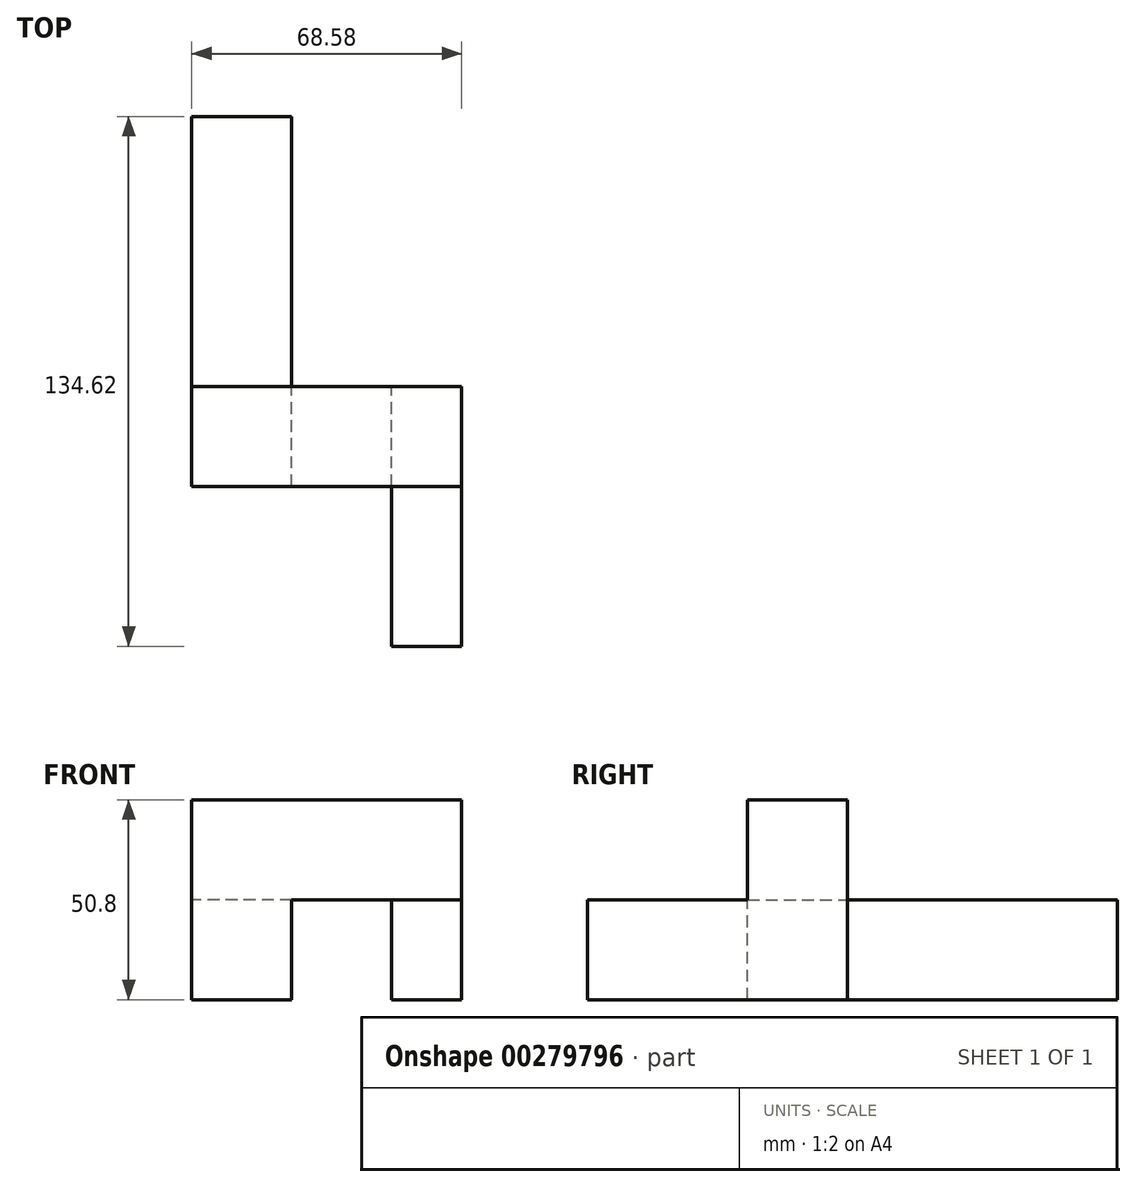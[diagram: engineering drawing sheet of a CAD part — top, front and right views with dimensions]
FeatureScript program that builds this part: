
annotation { "Feature Type Name" : "Feature", "Feature Type Description" : "" }
export const myFeature = defineFeature(function(context is Context, id is Id, definition is map)
    precondition{}
    {
        {
            var Q0;
            Q0=qCreatedBy(makeId("Right.planeOp"),FACE);
            var sketch = newSketch(context, id + "F0", { "sketchPlane" : qUnion([Q0])});
            skLineSegment(sketch, "E0.bottom", {"start": v(-70.78, -29.63) * mm, "end": v(-4.74, -29.63) * mm});
            skLineSegment(sketch, "E0.top", {"start": v(-70.78, -55.03) * mm, "end": v(-4.74, -55.03) * mm});
            skLineSegment(sketch, "E0.left", {"start": v(-70.78, -29.63) * mm, "end": v(-70.78, -55.03) * mm});
            skLineSegment(sketch, "E0.right", {"start": v(-4.74, -29.63) * mm, "end": v(-4.74, -55.03) * mm});
            skSolve(sketch);
        }
        {
            var Q0;
            Q0=makeQuery(id+"F0.imprint","IMPRINT",FACE,{"disambiguationData":[TD([[makeQuery(id+"F0.imprint","IMPRINT",EDGE,{"derivedFrom":sQuery(id+"F0.wireOp",EDGE,"E0.bottom")}),-1.0]])]});
            extrude(context, id + "F1", {"entities" : qUnion([Q0]), "oppositeDirection" : true, "depth" : 17.78 * mm});
        }
        {
            var Q0;
            Q0=makeQuery(id+"F1.opExtrude","SWEPT_FACE",FACE,{"disambiguationData":[OSD([sQuery(id+"F0.wireOp",EDGE,"E0.bottom")])]});
            var sketch = newSketch(context, id + "F2", { "sketchPlane" : qUnion([Q0])});
            skLineSegment(sketch, "E1", {"start": v(-17.78, -30.14) * mm, "end": v(0, -30.14) * mm});
            skSolve(sketch);
        }
        {
            var Q0;
            {var subQ0=sQuery(id+"F2.wireOp",EDGE,"E1");Q0=makeQuery(id+"F2.imprint","IMPRINT",FACE,{"disambiguationData":[TD([[makeQuery(id+"F2.imprint","IMPRINT",EDGE,{"derivedFrom":subQ0}),1.0]])]});}
            extrude(context, id + "F3", {"entities" : qUnion([Q0]), "operationType" : NewBodyOperationType.ADD, "depth" : 25.4 * mm});
        }
        {
            var Q0;
            {var subQ0=sQuery(id+"F0.wireOp",EDGE,"E0.bottom");var subQ1=makeQuery(id+"F1.opExtrude","CAP_EDGE",EDGE,{"disambiguationData":[OSD([subQ0])],"isStart":false});var subQ2=sQuery(id+"F0.wireOp",EDGE,"E0.right");Q0=makeQuery(id+"F3.boolean.opBoolean","MERGE",FACE,{"derivedFrom":[makeQuery(id+"F1.opExtrude","CAP_FACE",FACE,{"disambiguationData":[OSD([subQ0,sQuery(id+"F0.wireOp",EDGE,"E0.top"),sQuery(id+"F0.wireOp",EDGE,"E0.left"),subQ2])],"isStart":false}),makeQuery(id+"F3.opExtrude","SWEPT_FACE",FACE,{"disambiguationData":[OSD([subQ0]),TDD([makeQuery(id+"F2.imprint","IMPRINT",EDGE,{"disambiguationData":[TD([[makeQuery(id+"F2.imprint","INTERSECT",VERTEX,{"derivedFrom":[subQ1,sQuery(id+"F2.wireOp",EDGE,"E1")]}),-1.0]])],"derivedFrom":subQ1})])]})]});}
            var sketch = newSketch(context, id + "F4", { "sketchPlane" : qUnion([Q0])});
            skLineSegment(sketch, "E2", {"start": v(30.14, -29.63) * mm, "end": v(4.74, -29.63) * mm});
            skSolve(sketch);
        }
        {
            var Q0;
            {var subQ0=sQuery(id+"F4.wireOp",EDGE,"E2");Q0=makeQuery(id+"F4.imprint","IMPRINT",FACE,{"disambiguationData":[TD([[makeQuery(id+"F4.imprint","IMPRINT",EDGE,{"derivedFrom":subQ0}),-1.0]])]});}
            extrude(context, id + "F5", {"entities" : qUnion([Q0]), "operationType" : NewBodyOperationType.ADD, "depth" : 50.8 * mm});
        }
        {
            var Q0;
            Q0=makeQuery(id+"F5.opExtrude","SWEPT_FACE",FACE,{"disambiguationData":[OSD([sQuery(id+"F4.wireOp",EDGE,"E2")])]});
            var sketch = newSketch(context, id + "F6", { "sketchPlane" : qUnion([Q0])});
            skLineSegment(sketch, "E3", {"start": v(-43.18, 30.14) * mm, "end": v(-43.18, 4.74) * mm});
            skSolve(sketch);
        }
        {
            var Q0;
            {var subQ0=sQuery(id+"F6.wireOp",EDGE,"E3");Q0=makeQuery(id+"F6.imprint","IMPRINT",FACE,{"disambiguationData":[TD([[makeQuery(id+"F6.imprint","IMPRINT",EDGE,{"derivedFrom":subQ0}),-1.0]])]});}
            extrude(context, id + "F7", {"entities" : qUnion([Q0]), "operationType" : NewBodyOperationType.ADD, "depth" : 25.4 * mm});
        }
        {
            var Q0;
            {var subQ0=sQuery(id+"F0.wireOp",EDGE,"E0.right");var subQ1=sQuery(id+"F0.wireOp",EDGE,"E0.bottom");Q0=makeQuery(id+"F7.boolean.opBoolean","MERGE",FACE,{"derivedFrom":[makeQuery(id+"F5.boolean.opBoolean","MERGE",FACE,{"derivedFrom":[makeQuery(id+"F3.boolean.opBoolean","MERGE",FACE,{"derivedFrom":[makeQuery(id+"F1.opExtrude","SWEPT_FACE",FACE,{"disambiguationData":[OSD([subQ0])]}),makeQuery(id+"F3.opExtrude","SWEPT_FACE",FACE,{"disambiguationData":[OSD([subQ1,subQ0])]})]}),makeQuery(id+"F5.opExtrude","SWEPT_FACE",FACE,{"disambiguationData":[OSD([subQ1,subQ0])]})]}),makeQuery(id+"F7.opExtrude","SWEPT_FACE",FACE,{"disambiguationData":[OSD([subQ1,subQ0,sQuery(id+"F4.wireOp",EDGE,"E2")])]})]});}
            var sketch = newSketch(context, id + "F8", { "sketchPlane" : qUnion([Q0])});
            skLineSegment(sketch, "E4", {"start": v(43.18, -29.63) * mm, "end": v(68.58, -29.63) * mm});
            skSolve(sketch);
        }
        {
            var Q0;
            {var subQ0=sQuery(id+"F8.wireOp",EDGE,"E4");Q0=makeQuery(id+"F8.imprint","IMPRINT",FACE,{"disambiguationData":[TD([[makeQuery(id+"F8.imprint","IMPRINT",EDGE,{"derivedFrom":subQ0}),-1.0]])]});}
            extrude(context, id + "F9", {"entities" : qUnion([Q0]), "operationType" : NewBodyOperationType.ADD, "depth" : 68.58 * mm});
        }
    });
